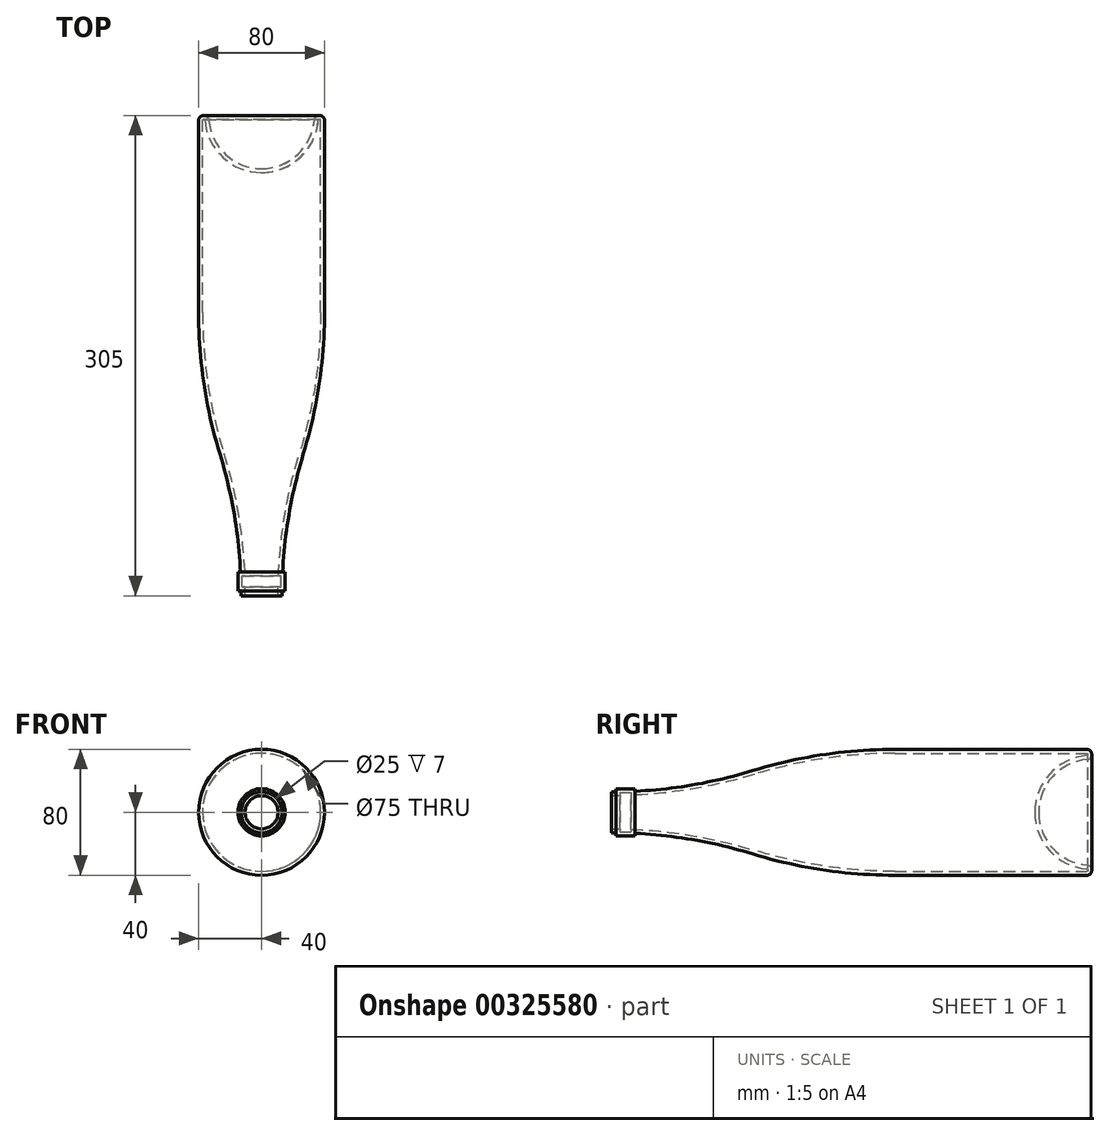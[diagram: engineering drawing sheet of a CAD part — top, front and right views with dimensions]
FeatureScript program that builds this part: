
annotation { "Feature Type Name" : "Feature", "Feature Type Description" : "" }
export const myFeature = defineFeature(function(context is Context, id is Id, definition is map)
    precondition{}
    {
        {
            var Q0;
            Q0=qCreatedBy(makeId("Top.planeOp"),FACE);
            var sketch = newSketch(context, id + "F0", { "sketchPlane" : qUnion([Q0])});
            skLineSegment(sketch, "E0.bottom", {"start": v(40, -152.5) * mm, "end": v(-40, -152.5) * mm, "construction": true});
            skLineSegment(sketch, "E0.top", {"start": v(40, 152.5) * mm, "end": v(-40, 152.5) * mm, "construction": true});
            skLineSegment(sketch, "E0.left", {"start": v(40, -152.5) * mm, "end": v(40, 152.5) * mm, "construction": true});
            skLineSegment(sketch, "E0.right", {"start": v(-40, -152.5) * mm, "end": v(-40, 152.5) * mm, "construction": true});
            skPoint(sketch, "E0.middle", {"position": v(0, 0) * mm});
            skLineSegment(sketch, "E1", {"start": v(0, 152.5) * mm, "end": v(0, -152.5) * mm, "construction": true});
            skLineSegment(sketch, "E2", {"start": v(13, -182.05) * mm, "end": v(13, -152.5) * mm, "construction": true});
            skPoint(sketch, "E3", {"position": v(40, 27.5) * mm});
            skArc(sketch, "E4", {"start": v(13, -152.5) * mm, "mid": v(16.4, -107) * mm, "end": v(26.5, -62.5) * mm});
            skArc(sketch, "E5", {"start": v(26.5, -62.5) * mm, "mid": v(36.6, -18) * mm, "end": v(40, 27.5) * mm});
            skLineSegment(sketch, "E6", {"start": v(40, 27.5) * mm, "end": v(40, 152.5) * mm});
            skArc(sketch, "E7", {"start": v(33.64, 152.5) * mm, "mid": v(23.78, 128.72) * mm, "end": v(0, 118.86) * mm});
            skLineSegment(sketch, "E8", {"start": v(40, 152.5) * mm, "end": v(33.64, 152.5) * mm});
            skLineSegment(sketch, "E9", {"start": v(13, -152.5) * mm, "end": v(0, -152.5) * mm});
            skLineSegment(sketch, "E10", {"start": v(0, 118.86) * mm, "end": v(0, -152.5) * mm});
            skLineSegment(sketch, "E11.bottom", {"start": v(13.01, -149.5) * mm, "end": v(15, -149.5) * mm});
            skLineSegment(sketch, "E11.top", {"start": v(13.37, -137.5) * mm, "end": v(15, -137.5) * mm});
            skLineSegment(sketch, "E11.right", {"start": v(15, -149.5) * mm, "end": v(15, -137.5) * mm});
            skSolve(sketch);
        }
        {
            var Q0;
            Q0 = qSketchRegion(id + "F0", true);
            var Q1;
            Q1=sQuery(id+"F0.wireOp",EDGE,"E1");
            revolve(context, id + "F1", {"entities" : qUnion([Q0]), "axis" : qUnion([Q1]), "revolveType" : RevolveType.FULL});
        }
        {
            var Q0;
            Q0=makeQuery(id+"F1.opRevolve","SWEPT_EDGE",EDGE,{"disambiguationData":[OSD([sQuery(id+"F0.wireOp",EDGE,"E6"),sQuery(id+"F0.wireOp",EDGE,"E8")])]});
            fillet(context, id + "F2", {"entities" : qUnion([Q0]), "radius" : 3 * mm, "tangentPropagation" : true, "allowEdgeOverflow" : false});
        }
        {
            var Q0;
            Q0=makeQuery(id+"F1.opRevolve","SWEPT_EDGE",EDGE,{"disambiguationData":[OSD([sQuery(id+"F0.wireOp",EDGE,"E7"),sQuery(id+"F0.wireOp",EDGE,"E8")])]});
            fillet(context, id + "F3", {"entities" : qUnion([Q0]), "radius" : 3 * mm, "tangentPropagation" : true, "allowEdgeOverflow" : false});
        }
        {
            var Q0;
            Q0=makeQuery(id+"F1.opRevolve","SWEPT_FACE",FACE,{"disambiguationData":[OSD([sQuery(id+"F0.wireOp",EDGE,"E9")])]});
            shell(context, id + "F4", {"entities" : qUnion([Q0]), "thickness" : 2.5 * mm});
        }
    });
